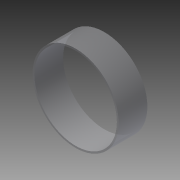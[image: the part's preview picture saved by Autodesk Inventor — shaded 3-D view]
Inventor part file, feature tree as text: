
AUTODESK INVENTOR PART (.ipt)
format: ipt  version: 2013 (Build 170138000, 138)  size: 107,008 bytes
history: native  units: in
note: dims shown in document units (in); Inventor stores cm internally (conversion verified against a paired STEP export)
features: extrude x3, sketch x3, plane x1
ambient origin geometry x8: Origin, YZ Plane, XZ Plane, XY Plane, X Axis, Y Axis, Z Axis, Center Point
bodies: Solid1 (feature_tree)
feature tree (7):
  extrude  "Extrusion1"  Depth=11.5in
  extrude  "Extrusion3"  Depth=1.5in TaperAngle=0.0deg
  plane  "Work Plane1"
  extrude  "Extrusion4"  Depth=0.75in
  sketch  "Sketch1"  dims[d0=12.0in d1=11.5in]
  sketch  "Sketch2"  dims[d2=4.0in d3=0.0in d6=1.5in d7=0.0in]
  sketch  "Sketch3"  dims[d8=1.0in d9=0.75in d10=0.1875in d11=4.0in d12=1.5in d13=0.0in]
